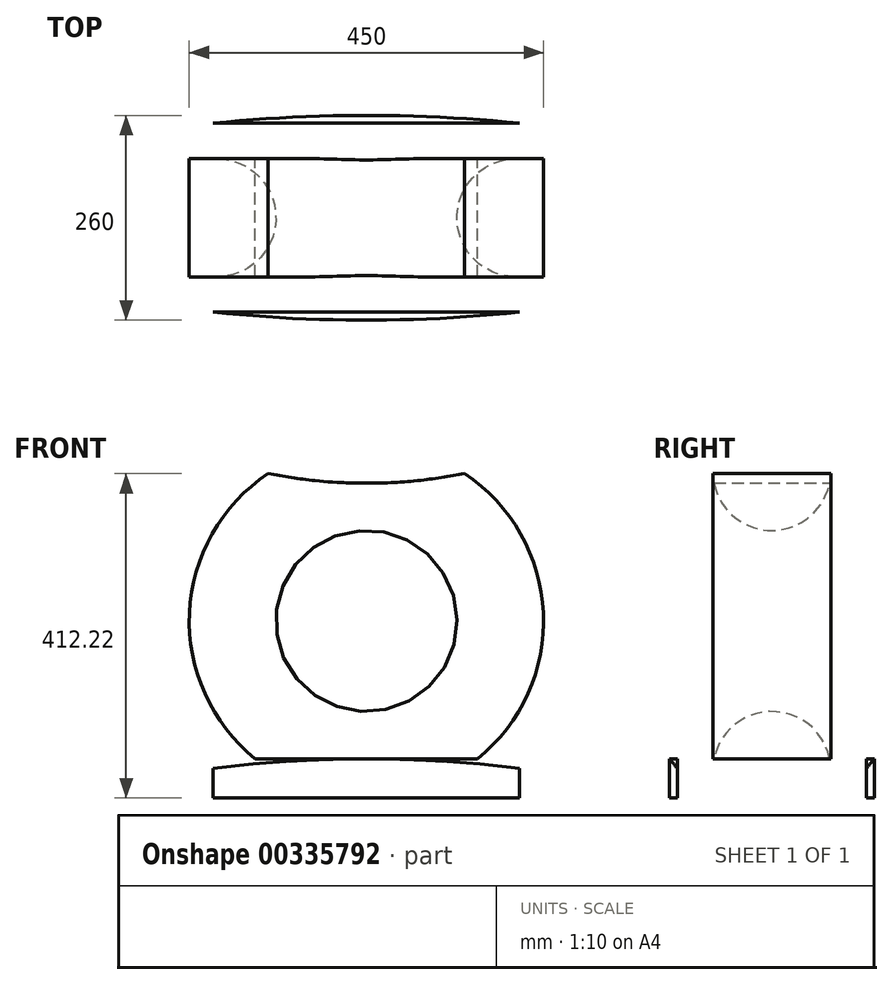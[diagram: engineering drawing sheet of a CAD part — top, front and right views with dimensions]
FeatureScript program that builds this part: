
annotation { "Feature Type Name" : "Feature", "Feature Type Description" : "" }
export const myFeature = defineFeature(function(context is Context, id is Id, definition is map)
    precondition{}
    {
        {
            var Q0;
            Q0=qCreatedBy(makeId("Front.planeOp"),FACE);
            var sketch = newSketch(context, id + "F0", { "sketchPlane" : qUnion([Q0])});
            skLineSegment(sketch, "E0", {"start": v(0, 550) * mm, "end": v(760, 550) * mm});
            skSolve(sketch);
        }
        {
            var Q0;
            Q0=qCreatedBy(makeId("Top.planeOp"),FACE);
            var sketch = newSketch(context, id + "F1", { "sketchPlane" : qUnion([Q0])});
            skLineSegment(sketch, "E1.left", {"start": v(105, -110) * mm, "end": v(105, 110) * mm});
            skLineSegment(sketch, "E1.right", {"start": v(655, -110) * mm, "end": v(655, 110) * mm});
            skLineSegment(sketch, "E2", {"start": v(380, -130) * mm, "end": v(380, 130) * mm});
            skArc(sketch, "E3", {"start": v(105, -110) * mm, "mid": v(380, -130) * mm, "end": v(655, -110) * mm});
            skPoint(sketch, "E4", {"position": v(105, 0) * mm});
            skArc(sketch, "E5", {"start": v(655, 110) * mm, "mid": v(380, 130) * mm, "end": v(105, 110) * mm});
            skPoint(sketch, "E6", {"position": v(655, 0) * mm});
            skSolve(sketch);
        }
        {
            var Q0;
            Q0=qSketchRegion(id+"F1",true);
            extrude(context, id + "F2", {"entities" : qUnion([Q0]), "depth" : 50 * mm});
        }
        {
            var Q0;
            Q0=makeQuery(id+"F2.opExtrude","CAP_EDGE",EDGE,{"disambiguationData":[OSD([sQuery(id+"F1.wireOp",EDGE,"E5")])],"isStart":false});
            cPoint(context, id + "F3", {"entities" : qUnion([Q0]), "parameter" : 0.5});
        }
        {
            var Q0;
            Q0=qCreatedBy(makeId("Right.planeOp"),FACE);
            var Q1;
            Q1=qCreatedBy(id+"F3",VERTEX);
            cPlane(context, id + "F4", {"entities" : qUnion([Q0, Q1]), "cplaneType" : CPlaneType.PLANE_POINT, "offset" : 25 * mm, "width" : 150 * mm, "height" : 150 * mm});
        }
        {
            var Q0;
            Q0=qCreatedBy(id+"F4.planeOp",FACE);
            var sketch = newSketch(context, id + "F5", { "sketchPlane" : qUnion([Q0])});
            skPoint(sketch, "E7", {"position": v(0, 0) * mm});
            skSolve(sketch);
        }
        {
            var Q0;
            Q0=qCreatedBy(makeId("Front.planeOp"),FACE);
            var sketch = newSketch(context, id + "F6", { "sketchPlane" : qUnion([Q0])});
            skCircle(sketch, "E8", {"center": v(380, 225) * mm, "radius": 225 * mm});
            skPoint(sketch, "E8.second.point", {"position": v(380, 0) * mm});
            skLineSegment(sketch, "E9.0", {"start": v(0, 0) * mm, "end": v(760, 0) * mm, "construction": true});
            skSolve(sketch);
        }
        {
            var Q0;
            Q0=qCreatedBy(id+"F4.planeOp",FACE);
            var sketch = newSketch(context, id + "F7", { "sketchPlane" : qUnion([Q0])});
            skLineSegment(sketch, "E10", {"start": v(40, 110) * mm, "end": v(-40, 110) * mm, "construction": true});
            skLineSegment(sketch, "E11", {"start": v(-75, 35) * mm, "end": v(-75, 0) * mm});
            skLineSegment(sketch, "E12", {"start": v(-75, 0) * mm, "end": v(75, 0) * mm});
            skLineSegment(sketch, "E13", {"start": v(75, 0) * mm, "end": v(75, 35) * mm});
            skPoint(sketch, "E14", {"position": v(0, 0) * mm});
            skLineSegment(sketch, "E15.0", {"start": v(-110, 50) * mm, "end": v(110, 50) * mm, "construction": true});
            skLineSegment(sketch, "E16", {"start": v(303.13, 225) * mm, "end": v(-310.09, 225) * mm, "construction": true});
            skArc(sketch, "E17", {"start": v(75, 35) * mm, "mid": v(0, 110) * mm, "end": v(-75, 35) * mm});
            skPoint(sketch, "E17.first.point", {"position": v(0, 110) * mm});
            skLineSegment(sketch, "E18", {"start": v(0, 110) * mm, "end": v(0, 0) * mm, "construction": true});
            skPoint(sketch, "E19.orphan", {"position": v(75, 20) * mm});
            skSolve(sketch);
        }
        {
            var Q0;
            Q0=qCreatedBy(id+"F4.planeOp",FACE);
            var sketch = newSketch(context, id + "F8", { "sketchPlane" : qUnion([Q0])});
            skLineSegment(sketch, "E20.0", {"start": v(303.13, 225) * mm, "end": v(-310.09, 225) * mm});
            skSolve(sketch);
        }
        {
            var Q0;
            Q0 = qSketchRegion(id + "F7", true);
            var Q1;
            Q1=sQuery(id+"F8.wireOp",EDGE,"E20.0");
            revolve(context, id + "F9", {"entities" : qUnion([Q0]), "axis" : qUnion([Q1]), "revolveType" : RevolveType.FULL});
        }
        {
            var Q0;
            Q0=qCreatedBy(makeId("Front.planeOp"),FACE);
            var sketch = newSketch(context, id + "F10", { "sketchPlane" : qUnion([Q0])});
            skArc(sketch, "E21", {"start": v(15.3, 550) * mm, "mid": v(380, 450) * mm, "end": v(744.7, 550) * mm});
            skPoint(sketch, "E22", {"position": v(380, 400) * mm});
            skLineSegment(sketch, "E23", {"start": v(15.3, 550) * mm, "end": v(0, 524.2) * mm});
            skLineSegment(sketch, "E24", {"start": v(0, 524.2) * mm, "end": v(760, 524.2) * mm, "construction": true});
            skLineSegment(sketch, "E25", {"start": v(760, 524.2) * mm, "end": v(744.7, 550) * mm});
            skArc(sketch, "E26", {"start": v(0, 524.2) * mm, "mid": v(380, 400) * mm, "end": v(760, 524.2) * mm});
            skLineSegment(sketch, "E27", {"start": v(380, 400) * mm, "end": v(380, 0) * mm, "construction": true});
            skSolve(sketch);
        }
        {
            var Q0;
            Q0=qSketchRegion(id+"F10",true);
            extrude(context, id + "F11", {"entities" : qUnion([Q0]), "depth" : 120 * mm, "hasSecondDirection" : true, "secondDirectionOppositeDirection" : true, "secondDirectionDepth" : 120 * mm});
        }
        {
            var Q0;
            Q0=qCreatedBy(makeId("Front.planeOp"),FACE);
            var sketch = newSketch(context, id + "F12", { "sketchPlane" : qUnion([Q0])});
            skArc(sketch, "E28", {"start": v(655, 25) * mm, "mid": v(380, 50) * mm, "end": v(105, 25) * mm});
            skLineSegment(sketch, "E29.0", {"start": v(105, 50) * mm, "end": v(105, 25) * mm});
            skLineSegment(sketch, "E29.1", {"start": v(655, 50) * mm, "end": v(105, 50) * mm});
            skLineSegment(sketch, "E29.2", {"start": v(655, 50) * mm, "end": v(655, 25) * mm});
            skPoint(sketch, "E30.orphan", {"position": v(655, 0) * mm});
            skPoint(sketch, "E31.orphan", {"position": v(105, 0) * mm});
            skSolve(sketch);
        }
        {
            var Q0;
            Q0=qSketchRegion(id+"F12",true);
            extrude(context, id + "F13", {"entities" : qUnion([Q0]), "operationType" : NewBodyOperationType.REMOVE, "oppositeDirection" : true, "depth" : 171 * mm, "hasSecondDirection" : true, "secondDirectionOppositeDirection" : false, "secondDirectionDepth" : 247 * mm});
        }
        {
            var Q0;
            Q0=qCreatedBy(makeId("Front.planeOp"),FACE);
            var sketch = newSketch(context, id + "F14", { "sketchPlane" : qUnion([Q0])});
            skLineSegment(sketch, "E32", {"start": v(105, 25) * mm, "end": v(105, 0) * mm});
            skLineSegment(sketch, "E33", {"start": v(105, 0) * mm, "end": v(655, 0) * mm});
            skLineSegment(sketch, "E34", {"start": v(655, 0) * mm, "end": v(655, 25) * mm});
            skLineSegment(sketch, "E35", {"start": v(0, 524.2) * mm, "end": v(0, 550) * mm});
            skLineSegment(sketch, "E36", {"start": v(760, 550) * mm, "end": v(760, 524.2) * mm});
            skArc(sketch, "E37.0", {"start": v(0, 524.2) * mm, "mid": v(380, 400) * mm, "end": v(760, 524.2) * mm});
            skArc(sketch, "E38.0", {"start": v(655, 25) * mm, "mid": v(380, 50) * mm, "end": v(105, 25) * mm});
            skLineSegment(sketch, "E39", {"start": v(760, 550) * mm, "end": v(0, 550) * mm});
            skSolve(sketch);
        }
        {
            var Q0;
            Q0=qSketchRegion(id+"F14",true);
            extrude(context, id + "F15", {"entities" : qUnion([Q0]), "operationType" : NewBodyOperationType.REMOVE, "depth" : 120 * mm, "hasSecondDirection" : true, "secondDirectionOppositeDirection" : true, "secondDirectionDepth" : 120 * mm});
        }
    });
